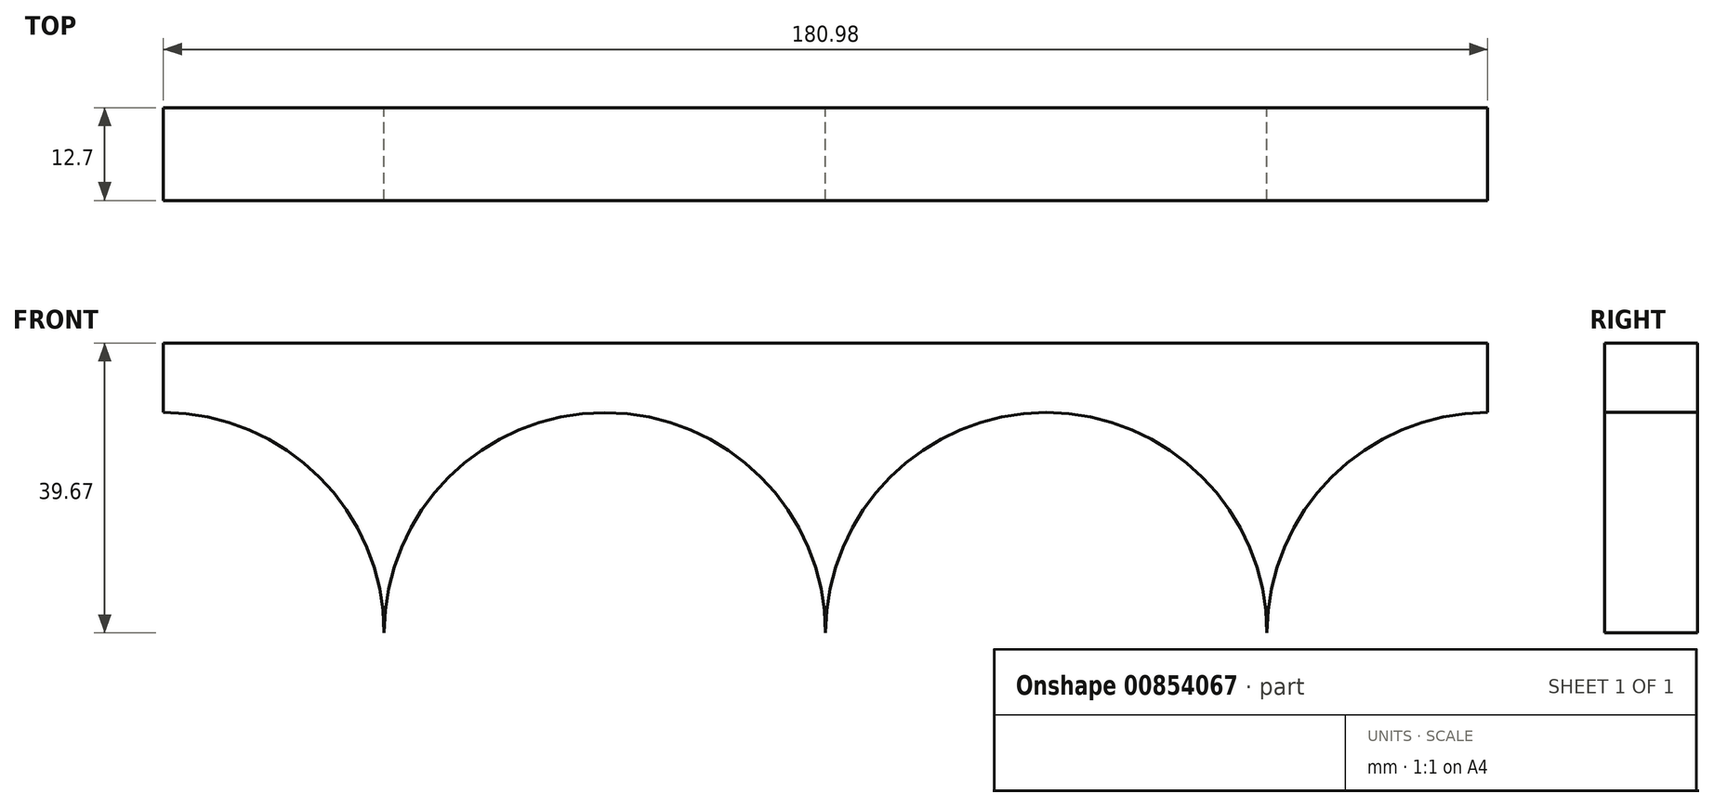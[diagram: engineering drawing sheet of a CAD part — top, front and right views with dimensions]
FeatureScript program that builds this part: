
annotation { "Feature Type Name" : "Feature", "Feature Type Description" : "" }
export const myFeature = defineFeature(function(context is Context, id is Id, definition is map)
    precondition{}
    {
        {
            var Q0;
            Q0=qCreatedBy(makeId("Front.planeOp"),FACE);
            var sketch = newSketch(context, id + "F0", { "sketchPlane" : qUnion([Q0])});
            skLineSegment(sketch, "E0.bottom", {"start": v(-90.49, -9.14) * mm, "end": v(90.49, -9.14) * mm});
            skLineSegment(sketch, "E0.top", {"start": v(-90.49, -48.81) * mm, "end": v(90.49, -48.81) * mm});
            skLineSegment(sketch, "E0.left", {"start": v(-90.49, -9.14) * mm, "end": v(-90.49, -48.81) * mm});
            skLineSegment(sketch, "E0.right", {"start": v(90.49, -9.14) * mm, "end": v(90.49, -48.81) * mm});
            skCircle(sketch, "E1", {"center": v(-30.16, -48.82) * mm, "radius": 30.16 * mm});
            skCircle(sketch, "E2", {"center": v(30.16, -48.81) * mm, "radius": 30.16 * mm});
            skCircle(sketch, "E3", {"center": v(-90.49, -48.81) * mm, "radius": 30.16 * mm});
            skCircle(sketch, "E4", {"center": v(90.49, -48.81) * mm, "radius": 30.16 * mm});
            skSolve(sketch);
        }
        {
            var Q0;
            {var subQ7=sQuery(id+"F0.wireOp",EDGE,"E0.bottom");Q0=makeQuery(id+"F0.imprint","IMPRINT",FACE,{"disambiguationData":[TD([[makeQuery(id+"F0.imprint","IMPRINT",EDGE,{"derivedFrom":subQ7}),-1.0]])]});}
            extrude(context, id + "F1", {"entities" : qUnion([Q0]), "depth" : 12.7 * mm, "offsetDistance" : 25.4 * mm});
        }
    });
